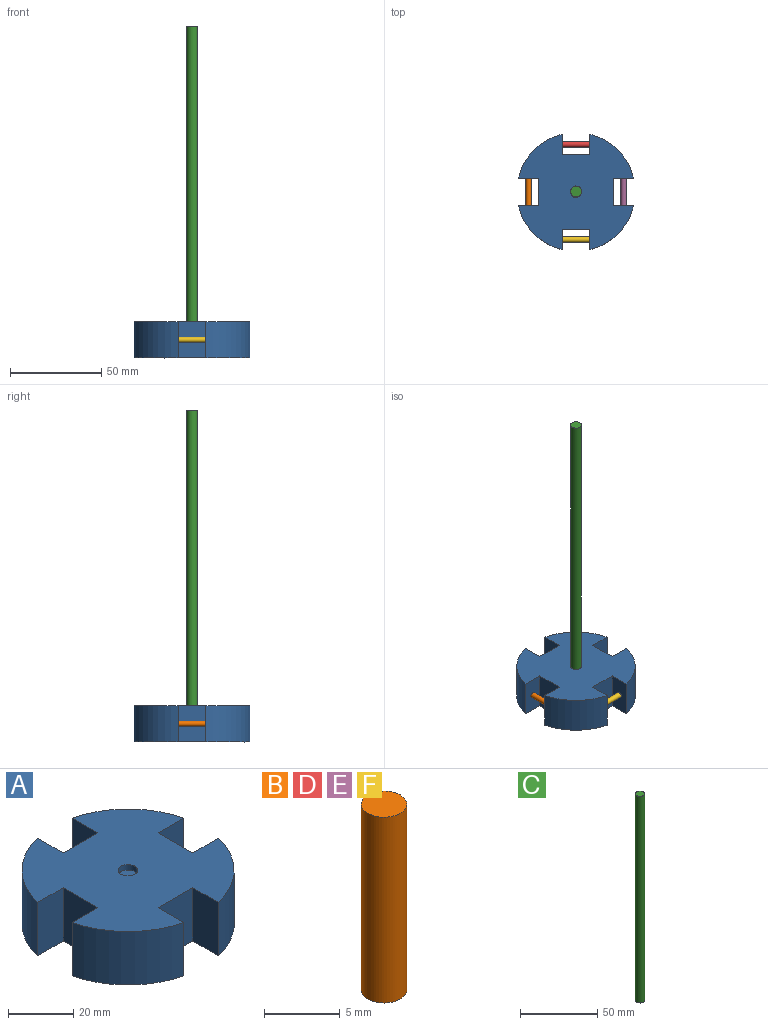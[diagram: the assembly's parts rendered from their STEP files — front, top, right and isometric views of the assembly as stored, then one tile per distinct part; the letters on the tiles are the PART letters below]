
ASSEMBLY  parts=6 mates=5
PART A: 20 faces, bbox 63.2x63.2x20 mm
  f0: plane 20x11.12mm, normal (-1,0,0), area 222.5mm2, adj f1,f15,f16,f17
  f1: plane 20x15mm, normal (0,1,0), area 300mm2, adj f0,f2,f16,f17
  f2: plane 20x11.12mm, normal (1,0,0), area 222.5mm2, adj f1,f3,f16,f17
  f3: cylinder r=32.5mm len=24.12mm, axis (0,0,1), area 718.3mm2, adj f2,f4,f16,f17
  f4: plane 20x11.12mm, normal (0,-1,0), area 222.5mm2, adj f3,f5,f16,f17
  f5: plane 20x15mm, normal (-1,0,0), area 300mm2, adj f4,f6,f16,f17
  f6: plane 20x11.12mm, normal (0,1,0), area 222.5mm2, adj f5,f7,f16,f17
  f7: cylinder r=32.5mm len=24.12mm, axis (0,0,1), area 718.3mm2, adj f6,f8,f16,f17
  f8: plane 20x11.12mm, normal (1,0,0), area 222.5mm2, adj f7,f9,f16,f17
  f9: plane 20x15mm, normal (0,-1,0), area 300mm2, adj f8,f10,f16,f17
  f10: plane 20x11.12mm, normal (-1,0,0), area 222.5mm2, adj f9,f11,f16,f17
  f11: cylinder r=32.5mm len=24.12mm, axis (0,0,1), area 718.3mm2, adj f10,f12,f16,f17
  f12: plane 20x11.12mm, normal (0,1,0), area 222.5mm2, adj f11,f13,f16,f17
  f13: plane 20x15mm, normal (1,0,0), area 300mm2, adj f12,f14,f16,f17
  f14: plane 20x11.12mm, normal (0,-1,0), area 222.5mm2, adj f13,f15,f16,f17
  f15: cylinder r=32.5mm len=24.12mm, axis (0,0,1), area 718.3mm2, adj f0,f14,f16,f17
  f16: plane 63.25x63.25mm, normal (0,0,-1), area 2615.8mm2, adj f0,f1,f2,f3,f4,f5,f6,f7
  f17: plane 63.25x63.25mm, normal (0,0,1), area 2587.5mm2, adj f0,f1,f2,f3,f4,f5,f6,f7
  f18: cylinder r=3mm len=6mm, axis (0,0,1), area 37.7mm2, adj f17,f19
  f19: plane 6x6mm, normal (0,0,1), area 28.3mm2, adj f18
PART B: 3 faces, bbox 3x3x15 mm
  f0: cylinder r=1.5mm len=15mm, axis (0,0,-1), area 141.4mm2, adj f1,f2
  f1: plane 3x3mm, normal (0,0,1), area 7.1mm2, adj f0
  f2: plane 3x3mm, normal (0,0,-1), area 7.1mm2, adj f0
PART C: 3 faces, bbox 6x6x164 mm
  f0: cylinder r=3mm len=164mm, axis (0,0,-1), area 3091.3mm2, adj f1,f2
  f1: plane 6x6mm, normal (0,0,1), area 28.3mm2, adj f0
  f2: plane 6x6mm, normal (0,0,-1), area 28.3mm2, adj f0
PART D: same geometry as B
PART E: same geometry as B
PART F: same geometry as B
PLACE A t=(10.76,-7.52,29.46)mm fixed
PLACE B rot(axis=(-1,0,0),90deg) t=(-15.3,-15.02,19.46)mm
PLACE C t=(10.76,-7.52,109.46)mm
PLACE D rot(axis=(-0.71,0,0.71),180deg) t=(18.26,18.54,19.46)mm
PLACE E rot(axis=(-1,0,0),90deg) t=(36.82,-15.02,19.46)mm
PLACE F rot(axis=(-0.71,0,-0.71),180deg) t=(3.26,-33.58,19.46)mm
MATE fastened B.f0 <-> A.f4  axis (0,1,0) through (-15.3,-0.02,19.46)mm
MATE fastened E.f0 <-> A.f14  axis (0,1,0) through (36.82,-0.02,19.46)mm
MATE fastened F.f0 <-> A.f10  axis (1,0,0) through (18.26,-33.58,19.46)mm
MATE fastened C.f0 <-> A.f18  axis (0,0,-1) through (10.76,-7.52,27.46)mm
MATE fastened D.f0 <-> A.f2  axis (-1,0,0) through (3.26,18.54,19.46)mm
